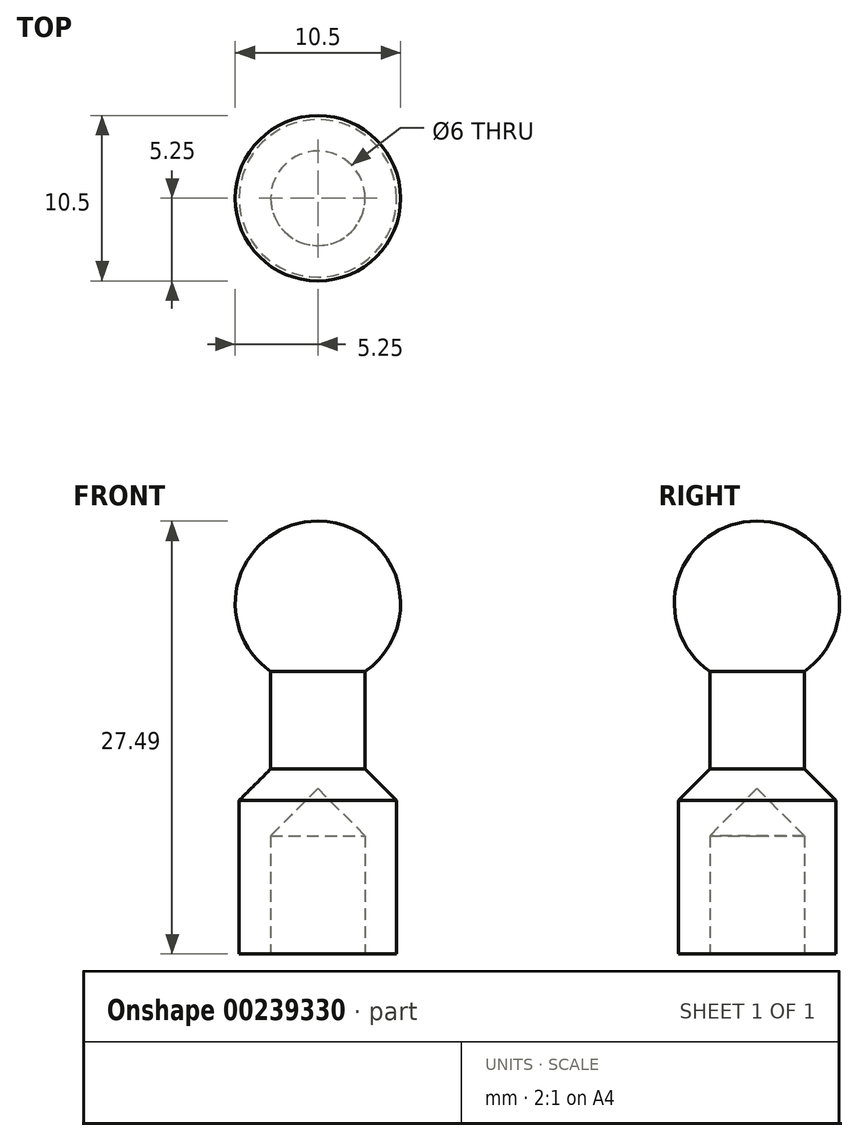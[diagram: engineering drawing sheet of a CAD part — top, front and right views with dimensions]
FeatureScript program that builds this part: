
annotation { "Feature Type Name" : "Feature", "Feature Type Description" : "" }
export const myFeature = defineFeature(function(context is Context, id is Id, definition is map)
    precondition{}
    {
        {
            var Q0;
            Q0=qCreatedBy(makeId("Front.planeOp"),FACE);
            var sketch = newSketch(context, id + "F0", { "sketchPlane" : qUnion([Q0])});
            skLineSegment(sketch, "E0", {"start": v(3, 0) * mm, "end": v(5, 0) * mm});
            skLineSegment(sketch, "E1", {"start": v(5, 0) * mm, "end": v(5, 9.74) * mm});
            skLineSegment(sketch, "E2", {"start": v(3, 0) * mm, "end": v(3, 7.5) * mm});
            skArc(sketch, "E3", {"start": v(3, 17.93) * mm, "mid": v(5, 23.81) * mm, "end": v(0, 27.5) * mm});
            skLineSegment(sketch, "E4", {"start": v(3, 7.5) * mm, "end": v(0, 10.5) * mm});
            skLineSegment(sketch, "E5", {"start": v(5, 9.74) * mm, "end": v(3, 11.74) * mm});
            skLineSegment(sketch, "E6", {"start": v(0, 0) * mm, "end": v(0, 27.5) * mm, "construction": true});
            skLineSegment(sketch, "E7", {"start": v(3, 11.74) * mm, "end": v(3, 17.93) * mm});
            skLineSegment(sketch, "E8", {"start": v(0, 10.5) * mm, "end": v(0, 27.5) * mm});
            skSolve(sketch);
        }
        {
            var Q0;
            Q0 = qSketchRegion(id + "F0", true);
            var Q1;
            Q1=sQuery(id+"F0.wireOp",EDGE,"E6");
            revolve(context, id + "F1", {"entities" : qUnion([Q0]), "axis" : qUnion([Q1]), "revolveType" : RevolveType.FULL});
        }
    });
